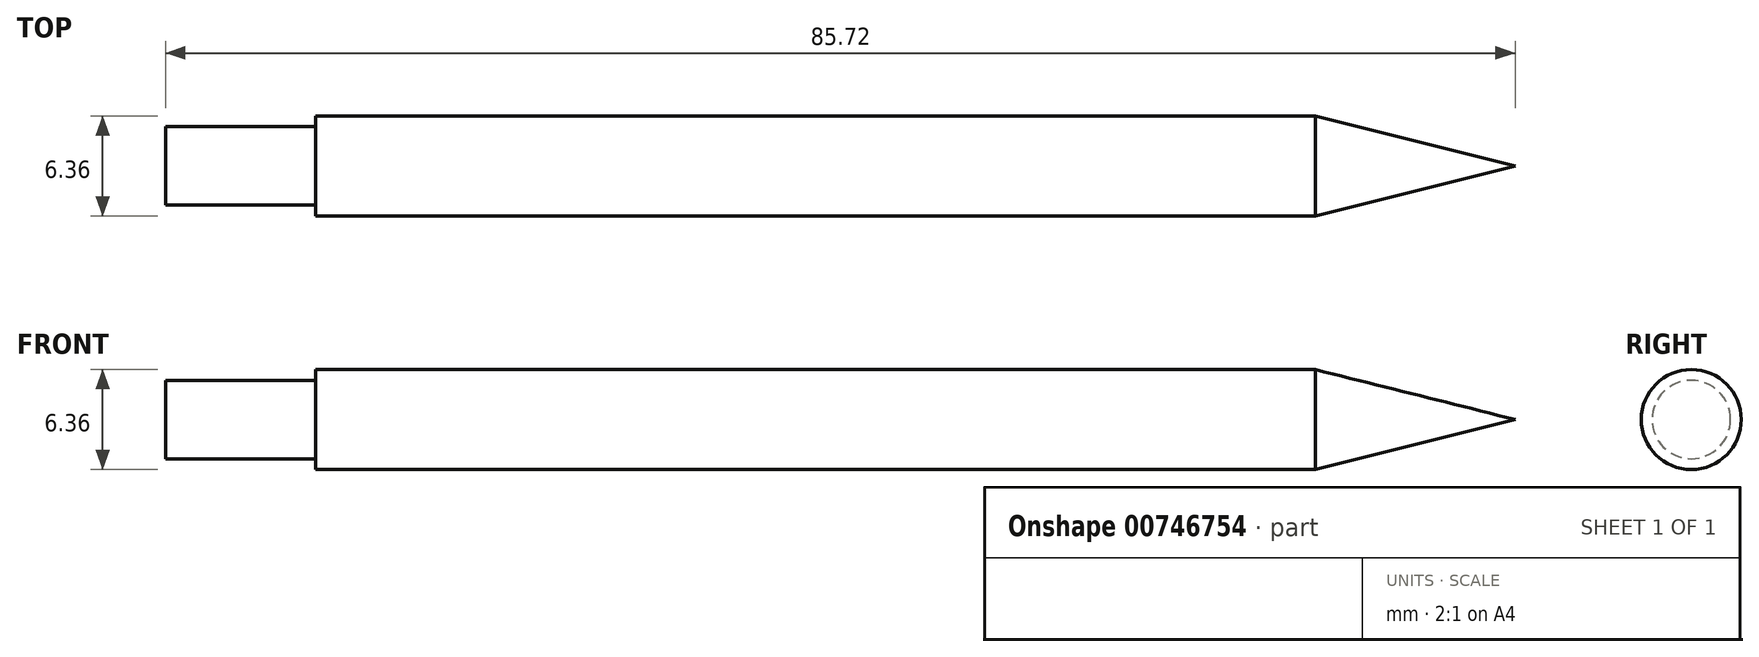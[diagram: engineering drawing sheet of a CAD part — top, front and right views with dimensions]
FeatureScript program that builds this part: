
annotation { "Feature Type Name" : "Feature", "Feature Type Description" : "" }
export const myFeature = defineFeature(function(context is Context, id is Id, definition is map)
    precondition{}
    {
        {
            var Q0;
            Q0=qCreatedBy(makeId("Front.planeOp"),FACE);
            var sketch = newSketch(context, id + "F0", { "sketchPlane" : qUnion([Q0])});
            skLineSegment(sketch, "E0", {"start": v(83.31, 0) * mm, "end": v(70.61, 3.18) * mm});
            skLineSegment(sketch, "E1", {"start": v(70.61, 3.18) * mm, "end": v(7.11, 3.18) * mm});
            skLineSegment(sketch, "E2", {"start": v(7.11, 3.18) * mm, "end": v(7.11, 2.49) * mm});
            skLineSegment(sketch, "E3", {"start": v(7.11, 2.49) * mm, "end": v(-2.41, 2.49) * mm});
            skLineSegment(sketch, "E4", {"start": v(-2.41, 2.49) * mm, "end": v(-2.41, 0) * mm});
            skLineSegment(sketch, "E5", {"start": v(-2.41, 0) * mm, "end": v(83.31, 0) * mm});
            skSolve(sketch);
        }
        {
            var Q0;
            Q0=makeQuery(id+"F0.imprint","IMPRINT",FACE,{"disambiguationData":[TD([[makeQuery(id+"F0.imprint","IMPRINT",EDGE,{"derivedFrom":sQuery(id+"F0.wireOp",EDGE,"E0")}),1.0]])]});
            var Q1;
            Q1=sQuery(id+"F0.wireOp",EDGE,"E5");
            revolve(context, id + "F1", {"surfaceOperationType" : NewSurfaceOperationType.NEW, "entities" : qUnion([Q0]), "axis" : qUnion([Q1]), "revolveType" : RevolveType.FULL});
        }
    });
